# Revit family: finalxxxFaucet-Kitchen-Grohe-Zedra-32298_Series
name_source: partatom
category: Plumbing Fixtures
units: mm (PartAtom-declared; Revit-internal decimal feet)

## family parameters
Always vertical = No
Cut with Voids When Loaded = No
OmniClass Number = 23.45.55.14
OmniClass Title = Single Faucets
Part Type = Normal
Room Calculation Point = No
Round Connector Dimension = Use Diameter
Shared = Yes
Work Plane-Based = Yes

## types (2) — shared parameters
ADA Compliant = Yes
Assembly Code = D2020300
CW Connection = No
CWFU = 1.5
CalGreen Compliant = Yes
Compliance Certifications = CEC Certified, Massachusetts Plumbing Board Approved, Low Lead Certified, CSA B125.1, NSF 61, CSA B125.1, Complies with lead plumbing laws & ASME A112.18.1
Default Elevation = 0"
Description = Single-Handle Pull Down Kitchen Faucet Triple Spray 1.75 GPM
Energy Policy Act of 1992 = Yes
Flow Rate = 1.75 gpm (6.6 L/min)
HW Connection = No
HWFU = 1.5
Height = 15 13/16"
Installation Instruction Link = https://americanstandard.box.com
Installation Type = Deck-Mounted
Length = 9 5/16"
Manufacturer = Grohe
Max. Hot Water Temp. = 158 °F
Min Max. Operating Pressure = 7.25 psi to 145 psi
Price = Prices may vary. Please consult Manufacturer Representative for most up-to-date price list.
Product Documentation Link = https://americanstandard.box.com
Product Page URL = https://www.grohe.us
Revised Date = 03/03/2022
Spout Height = 8 3/8"
Spout Reach = 9 5/16"
Tempered Water Connection = Yes
Tempered Water Connection Diameter = 3/8"
URL = https://www.grohe.us
Vent Connection = No
WFU = 2
Warranty Information = Lifetime limited warranty
Waste Connection = No
Width = 2 3/8"

## per-type parameters (varying)
| type | Finish | Material |
| 32298003 | Zinc-Grohe-003-StarLight Chrome | Zinc-Grohe-003-StarLight Chrome |
| 32298DC3 | Zinc-Grohe-DC3-SuperSteel Infinity Finish | Zinc-Grohe-DC3-SuperSteel Infinity Finish |

note: column(s) folded — value = type name in every type: Model

## geometry (parser evidence)
native form markers: Sweep x2
no freeform markers — native parametric forms only
